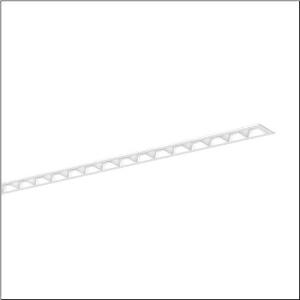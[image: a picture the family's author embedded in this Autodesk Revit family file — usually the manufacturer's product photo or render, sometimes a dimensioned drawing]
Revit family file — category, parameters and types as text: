
# Revit family: silica_r__21_51mx16db35wb_6bb0
name_source: partatom
category: Lighting Fixtures
units: mm (PartAtom-declared; Revit-internal decimal feet)

## family parameters
Cut with Voids When Loaded = No
Host = Face
Light Source = No
Part Type = Normal
Room Calculation Point = No
Round Connector Dimension = Use Diameter
Shared = No

## types (1)
- --- (1 x LED, 5400 lm, 31.4 W, 3000K)
    Apparent Load = 31 VA
    CIE Flux Codes = 83 98 100 100 100
    Color Rendering = 80
    Color Temperature = 3000K
    Default Elevation = 1800 mm
    Description = Silica® 21, office luminaire, primary light control with darklight reflector, of PMMA, white, CAT 2 (L<= 3000cd/m²), light emission: direct distribution, primary light characteristic: symmetric, installation type: recessed, LED, rated luminous flux: 5.400lm, luminous efficacy: 172lm/W, light colour: 830, colour temperature: 3000K, with terminal, 3+2-pole, max. 2.5mm², mains connection: 220..240V, AC, 50/60Hz, rated input power: 31.4W, luminaire housing, of aluminium, traffic white (RAL 9016), length: 1.528mm, width: 79mm, height: 53mm, protection rating (complete): IP20, insulation class (complete): insulation class I (protective earthing), certification: CE, permissible operating ambient temperature: 0..+35°C, standard: EN 50419, packaging unit: 1 piece
    Height = 0 mm  [stored 0 ft]
    Lamp = 1 x LED
    Lamp Light Flux = 5400 lm
    Lamp Power = 31.4 W
    Lamp count = 1
    Length = 1527 mm
    Luminous efficacy = 172 lm/W
    Manufacturer = Siteco
    ModVariant = No
    Model = 51MX16DB35WB
    Mounting Place = Ceiling
    Mounting Type = Recessed
    Number of Poles = 1
    OnlyDefault = Yes
    Power Factor = 1
    Product Name = Silica® 21
    Product group = office luminaire | ceiling recessed
    ProductGroupID = 400
    Protection Class = Protection class I
    Protection Degree = IP 20
    RLX_Detail_Level = 1
    RLX_Emergency_Light_Flux = 0 lm
    RLX_Emergency_Type = 0
    RLX_Emergency_Type_DB = No
    RlxData = <blob elided: 39721 chars, md5=99b6b199>
    Socket = socket
    Standby Power = 0 W
    System Light Flux = 5400 lm
    System Power = 31 W
    Type Comments = factory setting: luminous flux: 100 % | dim-lin: 254 | 360 mA
    Type Image = l_1335884.jpg
    URL = http://relux.com
    VarID = @adj_093923
    Voltage = 0 V
    Weight = 0.00 kg
    Width = 79 mm

note: [stored X ft] marks values corroborated as IEEE doubles in the binary element streams (Revit-internal decimal feet)

## geometry (parser evidence)
native form markers: Blend x4, Sweep x9
no freeform markers — native parametric forms only
